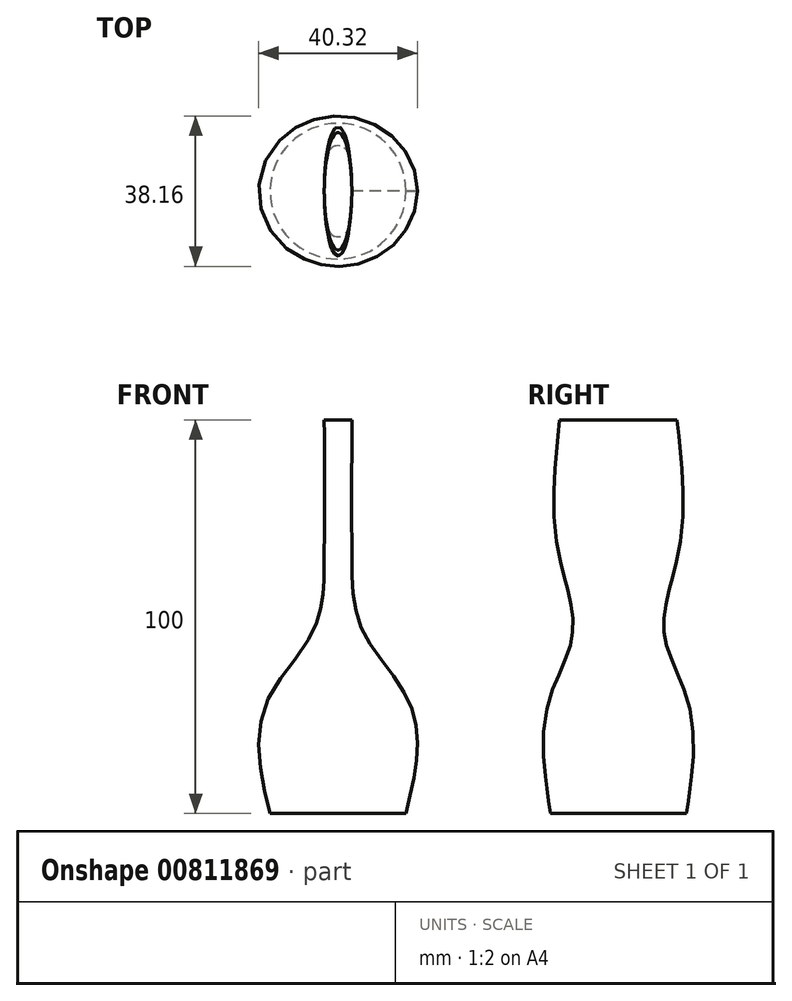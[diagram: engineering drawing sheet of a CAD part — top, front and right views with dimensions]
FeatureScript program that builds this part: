
annotation { "Feature Type Name" : "Feature", "Feature Type Description" : "" }
export const myFeature = defineFeature(function(context is Context, id is Id, definition is map)
    precondition{}
    {
        {
            var Q0;
            Q0=qCreatedBy(makeId("Top.planeOp"),FACE);
            var sketch = newSketch(context, id + "F0", { "sketchPlane" : qUnion([Q0])});
            skCircle(sketch, "E0", {"center": v(0, 0) * mm, "radius": 17.25 * mm});
            skSolve(sketch);
        }
        {
            var Q0;
            Q0=makeQuery(id+"F0.imprint","IMPRINT",FACE,{"disambiguationData":[TD([[makeQuery(id+"F0.imprint","IMPRINT",EDGE,{"derivedFrom":sQuery(id+"F0.wireOp",EDGE,"E0")}),1.0]])]});
            cPlane(context, id + "F1", {"entities" : qUnion([Q0]), "cplaneType" : CPlaneType.OFFSET, "offset" : 100 * mm, "width" : 150 * mm, "height" : 150 * mm});
        }
        {
            var Q0;
            Q0=qCreatedBy(id+"F1.planeOp",FACE);
            var sketch = newSketch(context, id + "F2", { "sketchPlane" : qUnion([Q0])});
            skEllipse(sketch, "E1", {"center": v(0, 0) * mm, "majorRadius": 14.93 * mm, "minorRadius": 3.5 * mm, "majorAxis": v(0, 1)});
            skSolve(sketch);
        }
        {
            var Q0;
            Q0=makeQuery(id+"F0.imprint","IMPRINT",FACE,{"disambiguationData":[TD([[makeQuery(id+"F0.imprint","IMPRINT",EDGE,{"derivedFrom":sQuery(id+"F0.wireOp",EDGE,"E0")}),1.0]])]});
            cPlane(context, id + "F3", {"entities" : qUnion([Q0]), "cplaneType" : CPlaneType.OFFSET, "offset" : 30 * mm, "width" : 150 * mm, "height" : 150 * mm});
        }
        {
            var Q0;
            Q0=qCreatedBy(id+"F3.planeOp",FACE);
            var sketch = newSketch(context, id + "F4", { "sketchPlane" : qUnion([Q0])});
            skCircle(sketch, "E2", {"center": v(0, 0) * mm, "radius": 17.25 * mm});
            skSolve(sketch);
        }
        {
            var Q0;
            Q0=makeQuery(id+"F4.imprint","IMPRINT",FACE,{"disambiguationData":[TD([[makeQuery(id+"F4.imprint","IMPRINT",EDGE,{"derivedFrom":sQuery(id+"F4.wireOp",EDGE,"E2")}),1.0]])]});
            cPlane(context, id + "F5", {"entities" : qUnion([Q0]), "cplaneType" : CPlaneType.OFFSET, "offset" : 15 * mm, "width" : 150 * mm, "height" : 150 * mm});
        }
        {
            var Q0;
            Q0=qCreatedBy(id+"F5.planeOp",FACE);
            var sketch = newSketch(context, id + "F6", { "sketchPlane" : qUnion([Q0])});
            skEllipse(sketch, "E3", {"center": v(0, 0) * mm, "majorRadius": 11.74 * mm, "minorRadius": 6.98 * mm, "majorAxis": v(0, 1)});
            skSolve(sketch);
        }
        {
            var Q0;
            Q0=makeQuery(id+"F6.imprint","IMPRINT",FACE,{"disambiguationData":[TD([[makeQuery(id+"F6.imprint","IMPRINT",EDGE,{"derivedFrom":sQuery(id+"F6.wireOp",EDGE,"E3")}),1.0]])]});
            cPlane(context, id + "F7", {"entities" : qUnion([Q0]), "cplaneType" : CPlaneType.OFFSET, "offset" : 20 * mm, "width" : 150 * mm, "height" : 150 * mm});
        }
        {
            var Q0;
            Q0=qCreatedBy(id+"F7.planeOp",FACE);
            var sketch = newSketch(context, id + "F8", { "sketchPlane" : qUnion([Q0])});
            skEllipse(sketch, "E4", {"center": v(0, 0) * mm, "majorRadius": 15 * mm, "minorRadius": 3.5 * mm, "majorAxis": v(0, 1)});
            skSolve(sketch);
        }
        {
            var Q0;
            Q0=makeQuery(id+"F0.imprint","IMPRINT",FACE,{"disambiguationData":[TD([[makeQuery(id+"F0.imprint","IMPRINT",EDGE,{"derivedFrom":sQuery(id+"F0.wireOp",EDGE,"E0")}),1.0]])]});
            var Q1;
            Q1=makeQuery(id+"F4.imprint","IMPRINT",FACE,{"disambiguationData":[TD([[makeQuery(id+"F4.imprint","IMPRINT",EDGE,{"derivedFrom":sQuery(id+"F4.wireOp",EDGE,"E2")}),1.0]])]});
            var Q2;
            Q2=makeQuery(id+"F6.imprint","IMPRINT",FACE,{"disambiguationData":[TD([[makeQuery(id+"F6.imprint","IMPRINT",EDGE,{"derivedFrom":sQuery(id+"F6.wireOp",EDGE,"E3")}),1.0]])]});
            var Q3;
            Q3=makeQuery(id+"F8.imprint","IMPRINT",FACE,{"disambiguationData":[TD([[makeQuery(id+"F8.imprint","IMPRINT",EDGE,{"derivedFrom":sQuery(id+"F8.wireOp",EDGE,"E4")}),1.0]])]});
            var Q4;
            Q4=makeQuery(id+"F2.imprint","IMPRINT",FACE,{"disambiguationData":[TD([[makeQuery(id+"F2.imprint","IMPRINT",EDGE,{"derivedFrom":sQuery(id+"F2.wireOp",EDGE,"E1")}),1.0]])]});
            loft(context, id + "F9", {"sheetProfilesArray" : [{ "sheetProfileEntities" : qUnion([Q0]) }, { "sheetProfileEntities" : qUnion([Q1]) }, { "sheetProfileEntities" : qUnion([Q2]) }, { "sheetProfileEntities" : qUnion([Q3]) }, { "sheetProfileEntities" : qUnion([Q4]) }]});
        }
    });
